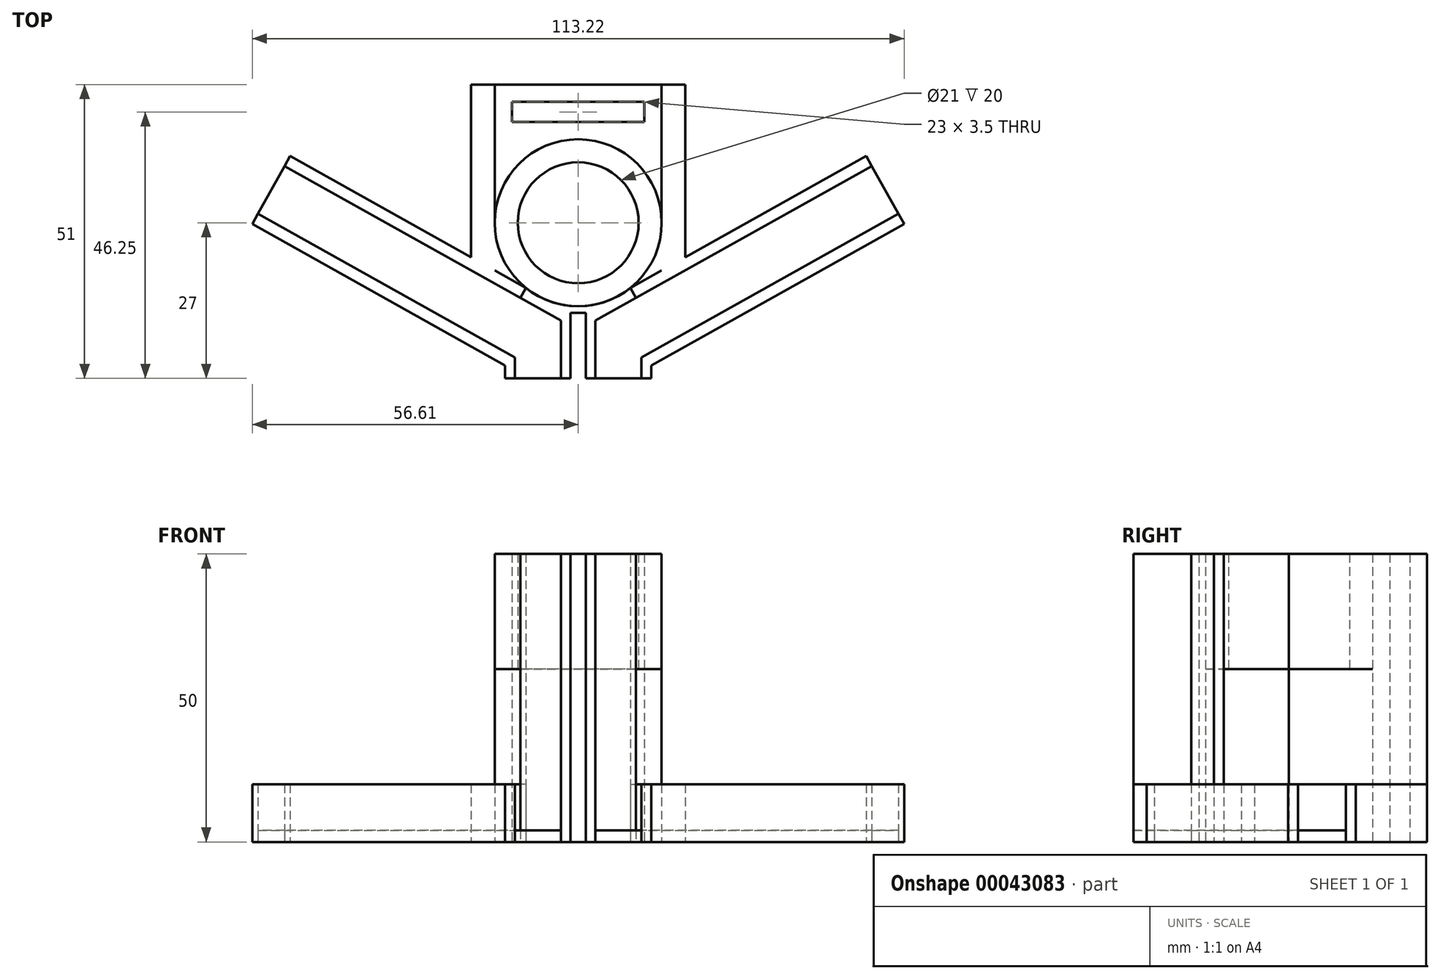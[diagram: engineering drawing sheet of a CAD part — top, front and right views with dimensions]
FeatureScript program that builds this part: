
annotation { "Feature Type Name" : "Feature", "Feature Type Description" : "" }
export const myFeature = defineFeature(function(context is Context, id is Id, definition is map)
    precondition{}
    {
        {
            var Q0;
            Q0=qCreatedBy(makeId("Top.planeOp"),FACE);
            var sketch = newSketch(context, id + "F0", { "sketchPlane" : qUnion([Q0])});
            skLineSegment(sketch, "E0", {"start": v(-3, 0) * mm, "end": v(-3, 10) * mm});
            skLineSegment(sketch, "E1", {"start": v(-3, 10) * mm, "end": v(-51, 36.85) * mm});
            skLineSegment(sketch, "E2", {"start": v(-51, 36.85) * mm, "end": v(-55.64, 28.56) * mm});
            skLineSegment(sketch, "E3", {"start": v(-55.64, 28.56) * mm, "end": v(-11, 3.59) * mm});
            skLineSegment(sketch, "E4", {"start": v(-11, 3.59) * mm, "end": v(-11, 0) * mm});
            skLineSegment(sketch, "E5", {"start": v(-11, 0) * mm, "end": v(-3, 0) * mm});
            skLineSegment(sketch, "E6", {"start": v(-3, 10) * mm, "end": v(-11, 3.59) * mm, "construction": true});
            skLineSegment(sketch, "E7", {"start": v(-11, 3.59) * mm, "end": v(-15.48, 0) * mm, "construction": true});
            skPoint(sketch, "E7.endSnap0", {"position": v(-7, 0) * mm});
            skLineSegment(sketch, "E8", {"start": v(-11, 0) * mm, "end": v(-15.48, 0) * mm, "construction": true});
            skLineSegment(sketch, "E9", {"start": v(-12.88, 2.08) * mm, "end": v(-3, 10) * mm, "construction": true});
            skLineSegment(sketch, "E10", {"start": v(-11, 0) * mm, "end": v(-12.68, 0) * mm});
            skLineSegment(sketch, "E11", {"start": v(-12.68, 0) * mm, "end": v(-12.68, 2.24) * mm});
            skLineSegment(sketch, "E12", {"start": v(-12.68, 2.24) * mm, "end": v(-56.61, 26.82) * mm});
            skLineSegment(sketch, "E13", {"start": v(-56.61, 26.82) * mm, "end": v(-55.64, 28.56) * mm});
            skLineSegment(sketch, "E14", {"start": v(-3, 0) * mm, "end": v(-1.32, 0) * mm});
            skLineSegment(sketch, "E15", {"start": v(-1.32, 0) * mm, "end": v(-1.32, 11.35) * mm});
            skLineSegment(sketch, "E16", {"start": v(-1.32, 11.35) * mm, "end": v(-50.02, 38.6) * mm});
            skLineSegment(sketch, "E17", {"start": v(-50.02, 38.6) * mm, "end": v(-51, 36.85) * mm});
            skLineSegment(sketch, "E18.MirrorCS", {"start": v(11, 0) * mm, "end": v(12.68, 0) * mm});
            skLineSegment(sketch, "E19.MirrorCS", {"start": v(3, 0) * mm, "end": v(1.32, 0) * mm});
            skLineSegment(sketch, "E20.MirrorCS", {"start": v(56.61, 26.82) * mm, "end": v(55.64, 28.56) * mm});
            skLineSegment(sketch, "E21.MirrorCS", {"start": v(12.68, 0) * mm, "end": v(12.68, 2.24) * mm});
            skLineSegment(sketch, "E22.MirrorCS", {"start": v(50.02, 38.6) * mm, "end": v(51, 36.85) * mm});
            skLineSegment(sketch, "E23.MirrorCS", {"start": v(11, 0) * mm, "end": v(15.48, 0) * mm});
            skLineSegment(sketch, "E24.MirrorCS", {"start": v(11, 3.59) * mm, "end": v(15.48, 0) * mm});
            skLineSegment(sketch, "E25.MirrorCS", {"start": v(11, 0) * mm, "end": v(3, 0) * mm});
            skLineSegment(sketch, "E26.MirrorCS", {"start": v(3, 10) * mm, "end": v(11, 3.59) * mm});
            skLineSegment(sketch, "E27.MirrorCS", {"start": v(3, 10) * mm, "end": v(51, 36.85) * mm});
            skLineSegment(sketch, "E28.MirrorCS", {"start": v(12.68, 2.24) * mm, "end": v(56.61, 26.82) * mm});
            skLineSegment(sketch, "E29.MirrorCS", {"start": v(1.32, 11.35) * mm, "end": v(50.02, 38.6) * mm});
            skLineSegment(sketch, "E30.MirrorCS", {"start": v(11, 3.59) * mm, "end": v(11, 0) * mm});
            skLineSegment(sketch, "E31.MirrorCS", {"start": v(51, 36.85) * mm, "end": v(55.64, 28.56) * mm});
            skLineSegment(sketch, "E32.MirrorCS", {"start": v(55.64, 28.56) * mm, "end": v(11, 3.59) * mm});
            skPoint(sketch, "E33.MirrorP", {"position": v(7, 0) * mm});
            skLineSegment(sketch, "E34.MirrorCS", {"start": v(1.32, 0) * mm, "end": v(1.32, 11.35) * mm});
            skLineSegment(sketch, "E35.MirrorCS", {"start": v(3, 0) * mm, "end": v(3, 10) * mm});
            skLineSegment(sketch, "E36.MirrorCS", {"start": v(12.88, 2.08) * mm, "end": v(3, 10) * mm});
            skLineSegment(sketch, "E37.bottom", {"start": v(-14.5, 51) * mm, "end": v(14.5, 51) * mm});
            skLineSegment(sketch, "E37.top", {"start": v(-14.5, 41.5) * mm, "end": v(14.5, 41.5) * mm});
            skLineSegment(sketch, "E37.left", {"start": v(-14.5, 51) * mm, "end": v(-14.5, 41.5) * mm});
            skLineSegment(sketch, "E37.right", {"start": v(14.5, 51) * mm, "end": v(14.5, 41.5) * mm});
            skLineSegment(sketch, "E38", {"start": v(0, 0) * mm, "end": v(0, 65.53) * mm, "construction": true});
            skPoint(sketch, "E39", {"position": v(0, 51) * mm});
            skLineSegment(sketch, "E40", {"start": v(-1.32, 11.35) * mm, "end": v(1.32, 11.35) * mm});
            skLineSegment(sketch, "E41", {"start": v(-1.32, 0) * mm, "end": v(1.32, 0) * mm});
            skCircle(sketch, "E42", {"center": v(0, 27) * mm, "radius": 10.5 * mm});
            skCircle(sketch, "E43", {"center": v(0, 27) * mm, "radius": 14.5 * mm});
            skPoint(sketch, "E44", {"position": v(0, 41.5) * mm});
            skLineSegment(sketch, "E45", {"start": v(-14.5, 27) * mm, "end": v(14.5, 27) * mm, "construction": true});
            skLineSegment(sketch, "E46.bottom", {"start": v(-14.5, 51) * mm, "end": v(-18.6, 51) * mm});
            skLineSegment(sketch, "E46.top", {"start": v(-14.5, 18.72) * mm, "end": v(-18.6, 18.72) * mm});
            skLineSegment(sketch, "E46.left", {"start": v(-14.5, 51) * mm, "end": v(-14.5, 18.72) * mm});
            skLineSegment(sketch, "E46.right", {"start": v(-18.6, 51) * mm, "end": v(-18.6, 18.72) * mm});
            skLineSegment(sketch, "E47.bottom", {"start": v(14.5, 51) * mm, "end": v(18.6, 51) * mm});
            skLineSegment(sketch, "E47.top", {"start": v(14.5, 18.72) * mm, "end": v(18.6, 18.72) * mm});
            skLineSegment(sketch, "E47.left", {"start": v(14.5, 51) * mm, "end": v(14.5, 18.72) * mm});
            skLineSegment(sketch, "E47.right", {"start": v(18.6, 51) * mm, "end": v(18.6, 18.72) * mm});
            skLineSegment(sketch, "E48", {"start": v(-9.07, 15.69) * mm, "end": v(-10.05, 13.94) * mm});
            skLineSegment(sketch, "E49", {"start": v(9.07, 15.69) * mm, "end": v(10.05, 13.94) * mm});
            skLineSegment(sketch, "E50.bottom", {"start": v(-11.5, 48) * mm, "end": v(11.5, 48) * mm});
            skLineSegment(sketch, "E50.top", {"start": v(-11.5, 44.5) * mm, "end": v(11.5, 44.5) * mm});
            skLineSegment(sketch, "E50.left", {"start": v(-11.5, 48) * mm, "end": v(-11.5, 44.5) * mm});
            skLineSegment(sketch, "E50.right", {"start": v(11.5, 48) * mm, "end": v(11.5, 44.5) * mm});
            skLineSegment(sketch, "E51", {"start": v(-11.5, 48) * mm, "end": v(-11.5, 51) * mm, "construction": true});
            skLineSegment(sketch, "E52", {"start": v(-11.5, 44.5) * mm, "end": v(-11.5, 41.5) * mm, "construction": true});
            skLineSegment(sketch, "E53", {"start": v(-11.5, 48) * mm, "end": v(-14.5, 48) * mm, "construction": true});
            skLineSegment(sketch, "E54", {"start": v(11.5, 48) * mm, "end": v(14.5, 48) * mm, "construction": true});
            skSolve(sketch);
        }
        {
            var Q0;
            Q0=makeQuery(id+"F0.imprint","IMPRINT",FACE,{"disambiguationData":[TD([[makeQuery(id+"F0.imprint","IMPRINT",EDGE,{"derivedFrom":sQuery(id+"F0.wireOp",EDGE,"E3")}),-1.0]])]});
            var Q1;
            {var subQ5=sQuery(id+"F0.wireOp",EDGE,"E17");Q1=makeQuery(id+"F0.imprint","IMPRINT",FACE,{"disambiguationData":[TD([[makeQuery(id+"F0.imprint","IMPRINT",EDGE,{"derivedFrom":subQ5}),1.0]])]});}
            var Q2;
            {var subQ3=sQuery(id+"F0.wireOp",EDGE,"E46.top");Q2=makeQuery(id+"F0.imprint","IMPRINT",FACE,{"disambiguationData":[TD([[makeQuery(id+"F0.imprint","IMPRINT",EDGE,{"derivedFrom":subQ3}),-1.0]])]});}
            var Q3;
            {var subQ3=sQuery(id+"F0.wireOp",EDGE,"E47.top");Q3=makeQuery(id+"F0.imprint","IMPRINT",FACE,{"disambiguationData":[TD([[makeQuery(id+"F0.imprint","IMPRINT",EDGE,{"derivedFrom":subQ3}),1.0]])]});}
            var Q4;
            Q4=makeQuery(id+"F0.imprint","IMPRINT",FACE,{"disambiguationData":[TD([[makeQuery(id+"F0.imprint","IMPRINT",EDGE,{"derivedFrom":sQuery(id+"F0.wireOp",EDGE,"E20.MirrorCS")}),1.0]])]});
            var Q5;
            {var subQ2=sQuery(id+"F0.wireOp",EDGE,"E21.MirrorCS");Q5=makeQuery(id+"F0.imprint","IMPRINT",FACE,{"disambiguationData":[TD([[makeQuery(id+"F0.imprint","IMPRINT",EDGE,{"derivedFrom":subQ2}),1.0]])]});}
            var Q6;
            {var subQ5=sQuery(id+"F0.wireOp",EDGE,"E22.MirrorCS");Q6=makeQuery(id+"F0.imprint","IMPRINT",FACE,{"disambiguationData":[TD([[makeQuery(id+"F0.imprint","IMPRINT",EDGE,{"derivedFrom":subQ5}),-1.0]])]});}
            var Q7;
            {var subQ6=sQuery(id+"F0.wireOp",EDGE,"E46.bottom");Q7=makeQuery(id+"F0.imprint","IMPRINT",FACE,{"disambiguationData":[TD([[makeQuery(id+"F0.imprint","IMPRINT",EDGE,{"derivedFrom":subQ6}),1.0]])]});}
            var Q8;
            {var subQ3=sQuery(id+"F0.wireOp",EDGE,"E47.bottom");Q8=makeQuery(id+"F0.imprint","IMPRINT",FACE,{"disambiguationData":[TD([[makeQuery(id+"F0.imprint","IMPRINT",EDGE,{"derivedFrom":subQ3}),-1.0]])]});}
            var Q9;
            {var subQ1=sQuery(id+"F0.wireOp",EDGE,"E46.top");Q9=makeQuery(id+"F0.imprint","IMPRINT",FACE,{"disambiguationData":[TD([[makeQuery(id+"F0.imprint","IMPRINT",EDGE,{"derivedFrom":subQ1}),1.0]])]});}
            var Q10;
            {var subQ0=sQuery(id+"F0.wireOp",EDGE,"E47.top");Q10=makeQuery(id+"F0.imprint","IMPRINT",FACE,{"disambiguationData":[TD([[makeQuery(id+"F0.imprint","IMPRINT",EDGE,{"derivedFrom":subQ0}),-1.0]])]});}
            extrude(context, id + "F1", {"entities" : qUnion([Q0, Q1, Q2, Q3, Q4, Q5, Q6, Q7, Q8, Q9, Q10]), "depth" : 10 * mm});
        }
        {
            var Q0;
            {var subQ0=sQuery(id+"F0.wireOp",EDGE,"E0");Q0=makeQuery(id+"F0.imprint","IMPRINT",FACE,{"disambiguationData":[TD([[makeQuery(id+"F0.imprint","IMPRINT",EDGE,{"derivedFrom":subQ0}),1.0]])]});}
            var Q1;
            {var subQ5=sQuery(id+"F0.wireOp",EDGE,"E31.MirrorCS");Q1=makeQuery(id+"F0.imprint","IMPRINT",FACE,{"disambiguationData":[TD([[makeQuery(id+"F0.imprint","IMPRINT",EDGE,{"derivedFrom":subQ5}),-1.0]])]});}
            var Q2;
            Q2=makeQuery(id+"F0.imprint","IMPRINT",FACE,{"disambiguationData":[TD([[makeQuery(id+"F0.imprint","IMPRINT",EDGE,{"derivedFrom":sQuery(id+"F0.wireOp",EDGE,"E25.MirrorCS")}),-1.0]])]});
            extrude(context, id + "F2", {"entities" : qUnion([Q0, Q1, Q2]), "depth" : 2 * mm});
        }
        {
            var Q0;
            Q0=makeQuery(id+"F0.imprint","IMPRINT",FACE,{"disambiguationData":[TD([[makeQuery(id+"F0.imprint","IMPRINT",EDGE,{"derivedFrom":sQuery(id+"F0.wireOp",EDGE,"E42")}),-1.0]])]});
            var Q1;
            {var subQ0=sQuery(id+"F0.wireOp",EDGE,"E43");var subQ1=sQuery(id+"F0.wireOp",EDGE,"E16");var subQ3=makeQuery(id+"F0.imprint","INTERSECT",VERTEX,{"disambiguationData":[OD(0.0)],"derivedFrom":[subQ1,subQ0]});Q1=makeQuery(id+"F0.imprint","IMPRINT",FACE,{"disambiguationData":[TD([[makeQuery(id+"F0.imprint","IMPRINT",EDGE,{"disambiguationData":[TD([[subQ3,-1.0]])],"derivedFrom":subQ1}),1.0]])]});}
            var Q2;
            {var subQ0=sQuery(id+"F0.wireOp",EDGE,"E43");var subQ1=sQuery(id+"F0.wireOp",EDGE,"E29.MirrorCS");var subQ3=makeQuery(id+"F0.imprint","INTERSECT",VERTEX,{"disambiguationData":[OD(0.0)],"derivedFrom":[subQ1,subQ0]});Q2=makeQuery(id+"F0.imprint","IMPRINT",FACE,{"disambiguationData":[TD([[makeQuery(id+"F0.imprint","IMPRINT",EDGE,{"disambiguationData":[TD([[subQ3,-1.0]])],"derivedFrom":subQ1}),-1.0]])]});}
            extrude(context, id + "F3", {"entities" : qUnion([Q0, Q1, Q2]), "depth" : 50 * mm});
        }
        {
            var Q0;
            Q0=makeQuery(id+"F0.imprint","IMPRINT",FACE,{"disambiguationData":[TD([[makeQuery(id+"F0.imprint","IMPRINT",EDGE,{"derivedFrom":sQuery(id+"F0.wireOp",EDGE,"E42")}),-1.0]])]});
            var Q1;
            {var subQ0=sQuery(id+"F0.wireOp",EDGE,"E43");var subQ1=sQuery(id+"F0.wireOp",EDGE,"E16");var subQ3=makeQuery(id+"F0.imprint","INTERSECT",VERTEX,{"disambiguationData":[OD(0.0)],"derivedFrom":[subQ1,subQ0]});Q1=makeQuery(id+"F0.imprint","IMPRINT",FACE,{"disambiguationData":[TD([[makeQuery(id+"F0.imprint","IMPRINT",EDGE,{"disambiguationData":[TD([[subQ3,-1.0]])],"derivedFrom":subQ1}),1.0]])]});}
            var Q2;
            {var subQ0=sQuery(id+"F0.wireOp",EDGE,"E43");var subQ1=sQuery(id+"F0.wireOp",EDGE,"E29.MirrorCS");var subQ3=makeQuery(id+"F0.imprint","INTERSECT",VERTEX,{"disambiguationData":[OD(0.0)],"derivedFrom":[subQ1,subQ0]});Q2=makeQuery(id+"F0.imprint","IMPRINT",FACE,{"disambiguationData":[TD([[makeQuery(id+"F0.imprint","IMPRINT",EDGE,{"disambiguationData":[TD([[subQ3,-1.0]])],"derivedFrom":subQ1}),-1.0]])]});}
            extrude(context, id + "F4", {"entities" : qUnion([Q0, Q1, Q2]), "operationType" : NewBodyOperationType.REMOVE, "depth" : 30 * mm});
        }
        {
            var Q0;
            {var subQ1=sQuery(id+"F0.wireOp",EDGE,"E46.left");var subQ3=sQuery(id+"F0.wireOp",EDGE,"E37.top");var subQ5=makeQuery(id+"F0.imprint","INTERSECT",VERTEX,{"derivedFrom":[subQ3,subQ1]});Q0=makeQuery(id+"F0.imprint","IMPRINT",FACE,{"disambiguationData":[TD([[makeQuery(id+"F0.imprint","IMPRINT",EDGE,{"disambiguationData":[TD([[subQ5,-1.0]])],"derivedFrom":subQ3}),-1.0]])]});}
            var Q1;
            {var subQ0=sQuery(id+"F0.wireOp",EDGE,"E47.left");var subQ3=sQuery(id+"F0.wireOp",EDGE,"E37.top");var subQ4=makeQuery(id+"F0.imprint","INTERSECT",VERTEX,{"derivedFrom":[subQ3,subQ0]});Q1=makeQuery(id+"F0.imprint","IMPRINT",FACE,{"disambiguationData":[TD([[makeQuery(id+"F0.imprint","IMPRINT",EDGE,{"disambiguationData":[TD([[subQ4,1.0]])],"derivedFrom":subQ3}),-1.0]])]});}
            var Q2;
            {var subQ5=sQuery(id+"F0.wireOp",EDGE,"E40");Q2=makeQuery(id+"F0.imprint","IMPRINT",FACE,{"disambiguationData":[TD([[makeQuery(id+"F0.imprint","IMPRINT",EDGE,{"derivedFrom":subQ5}),1.0]])]});}
            var Q3;
            {var subQ3=sQuery(id+"F0.wireOp",EDGE,"E37.bottom");Q3=makeQuery(id+"F0.imprint","IMPRINT",FACE,{"disambiguationData":[TD([[makeQuery(id+"F0.imprint","IMPRINT",EDGE,{"derivedFrom":subQ3}),-1.0]])]});}
            var Q4;
            Q4=makeQuery(id+"F0.imprint","IMPRINT",FACE,{"disambiguationData":[TD([[makeQuery(id+"F0.imprint","IMPRINT",EDGE,{"derivedFrom":sQuery(id+"F0.wireOp",EDGE,"E19.MirrorCS")}),-1.0]])]});
            var Q5;
            {var subQ5=sQuery(id+"F0.wireOp",EDGE,"E0");Q5=makeQuery(id+"F0.imprint","IMPRINT",FACE,{"disambiguationData":[TD([[makeQuery(id+"F0.imprint","IMPRINT",EDGE,{"derivedFrom":subQ5}),-1.0]])]});}
            extrude(context, id + "F5", {"entities" : qUnion([Q0, Q1, Q2, Q3, Q4, Q5]), "depth" : 50 * mm});
        }
    });
